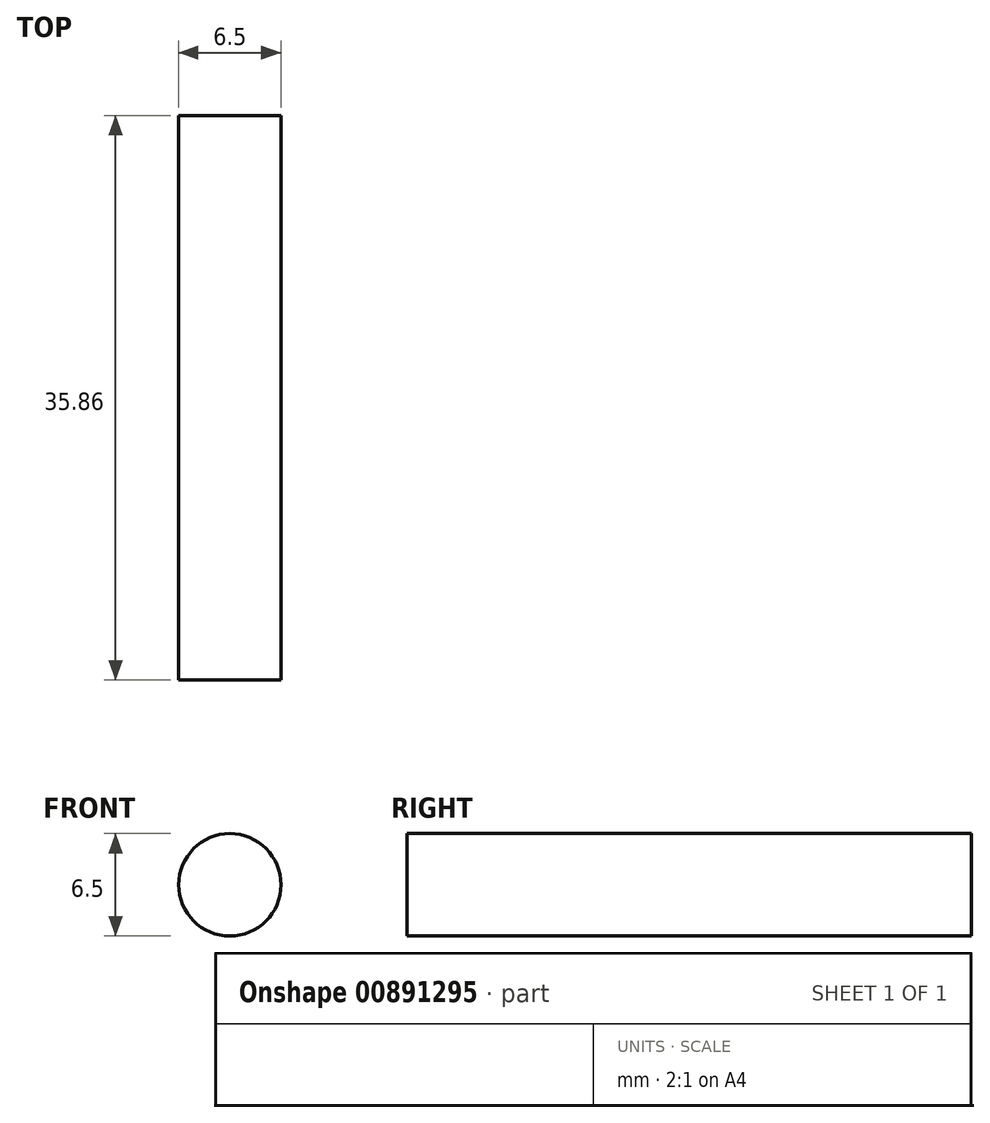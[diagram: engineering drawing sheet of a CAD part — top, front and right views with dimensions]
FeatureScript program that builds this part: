
annotation { "Feature Type Name" : "Feature", "Feature Type Description" : "" }
export const myFeature = defineFeature(function(context is Context, id is Id, definition is map)
    precondition{}
    {
        {
            var Q0;
            Q0=qCreatedBy(makeId("Front.planeOp"),FACE);
            var sketch = newSketch(context, id + "F0", { "sketchPlane" : qUnion([Q0])});
            skCircle(sketch, "E0", {"center": v(0, 0) * mm, "radius": 3.25 * mm});
            skSolve(sketch);
        }
        {
            var Q0;
            Q0 = qSketchRegion(id + "F0", true);
            extrude(context, id + "F1", {"entities" : qUnion([Q0]), "endBound" : BoundingType.SYMMETRIC, "depth" : 35.85 * mm, "offsetDistance" : 25 * mm});
        }
    });
